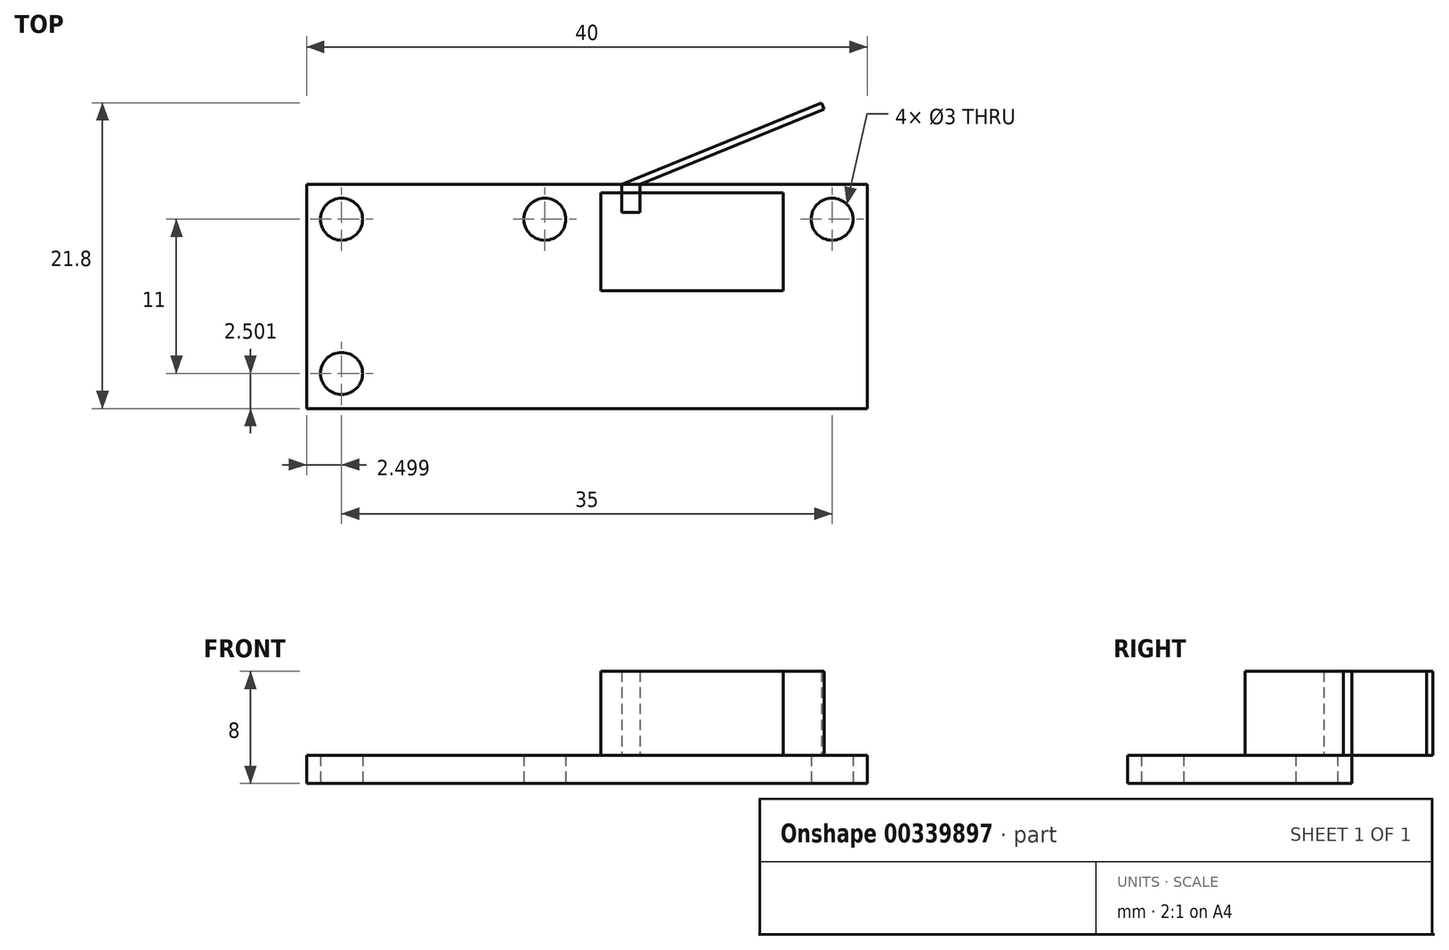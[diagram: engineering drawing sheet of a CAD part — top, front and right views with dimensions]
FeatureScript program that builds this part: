
annotation { "Feature Type Name" : "Feature", "Feature Type Description" : "" }
export const myFeature = defineFeature(function(context is Context, id is Id, definition is map)
    precondition{}
    {
        {
            var Q0;
            Q0=qCreatedBy(makeId("Top.planeOp"),FACE);
            var sketch = newSketch(context, id + "F0", { "sketchPlane" : qUnion([Q0])});
            skLineSegment(sketch, "E0.bottom", {"start": v(-12.98, 9.23) * mm, "end": v(27.02, 9.23) * mm});
            skLineSegment(sketch, "E0.top", {"start": v(-12.98, -6.77) * mm, "end": v(27.02, -6.77) * mm});
            skLineSegment(sketch, "E0.left", {"start": v(-12.98, 9.23) * mm, "end": v(-12.98, -6.77) * mm});
            skLineSegment(sketch, "E0.right", {"start": v(27.02, 9.23) * mm, "end": v(27.02, -6.77) * mm});
            skCircle(sketch, "E1", {"center": v(24.52, 6.73) * mm, "radius": 1.5 * mm});
            skCircle(sketch, "E2", {"center": v(4.02, 6.73) * mm, "radius": 1.5 * mm});
            skCircle(sketch, "E3", {"center": v(-10.48, 6.73) * mm, "radius": 1.5 * mm});
            skCircle(sketch, "E4", {"center": v(-10.48, -4.27) * mm, "radius": 1.5 * mm});
            skLineSegment(sketch, "E5", {"start": v(-12.98, 6.73) * mm, "end": v(27.02, 6.73) * mm, "construction": true});
            skLineSegment(sketch, "E6", {"start": v(-10.48, 9.23) * mm, "end": v(-10.48, -6.77) * mm, "construction": true});
            skSolve(sketch);
        }
        {
            var Q0;
            Q0=makeQuery(id+"F0.imprint","IMPRINT",FACE,{"disambiguationData":[TD([[makeQuery(id+"F0.imprint","IMPRINT",EDGE,{"derivedFrom":sQuery(id+"F0.wireOp",EDGE,"E0.bottom")}),-1.0]])]});
            extrude(context, id + "F1", {"entities" : qUnion([Q0]), "depth" : 2 * mm, "offsetDistance" : 25 * mm});
        }
        {
            var Q0;
            Q0=makeQuery(id+"F1.opExtrude","CAP_FACE",FACE,{"disambiguationData":[OSD([sQuery(id+"F0.wireOp",EDGE,"E0.bottom"),sQuery(id+"F0.wireOp",EDGE,"E0.top"),sQuery(id+"F0.wireOp",EDGE,"E0.left"),sQuery(id+"F0.wireOp",EDGE,"E0.right"),sQuery(id+"F0.wireOp",EDGE,"E1"),sQuery(id+"F0.wireOp",EDGE,"E2"),sQuery(id+"F0.wireOp",EDGE,"E3"),sQuery(id+"F0.wireOp",EDGE,"E4")])],"isStart":false});
            var sketch = newSketch(context, id + "F2", { "sketchPlane" : qUnion([Q0])});
            skLineSegment(sketch, "E7.bottom", {"start": v(8.02, 8.63) * mm, "end": v(21.02, 8.63) * mm});
            skLineSegment(sketch, "E7.top", {"start": v(8.02, 1.63) * mm, "end": v(21.02, 1.63) * mm});
            skLineSegment(sketch, "E7.left", {"start": v(8.02, 8.63) * mm, "end": v(8.02, 1.63) * mm});
            skLineSegment(sketch, "E7.right", {"start": v(21.02, 8.63) * mm, "end": v(21.02, 1.63) * mm});
            skLineSegment(sketch, "E8.bottom", {"start": v(-12.26, 7.1) * mm, "end": v(-2.26, 7.1) * mm});
            skLineSegment(sketch, "E8.top", {"start": v(-12.26, -4.9) * mm, "end": v(-2.26, -4.9) * mm});
            skLineSegment(sketch, "E8.left", {"start": v(-12.26, 7.1) * mm, "end": v(-12.26, -4.9) * mm});
            skLineSegment(sketch, "E8.right", {"start": v(-2.26, 7.1) * mm, "end": v(-2.26, -4.9) * mm});
            skLineSegment(sketch, "E9", {"start": v(8.02, 8.63) * mm, "end": v(23.77, 15.03) * mm});
            skLineSegment(sketch, "E10", {"start": v(23.77, 15.03) * mm, "end": v(23.96, 14.57) * mm});
            skLineSegment(sketch, "E11", {"start": v(23.96, 14.57) * mm, "end": v(9.32, 8.63) * mm});
            skSolve(sketch);
        }
        {
            var Q0;
            {var subQ0=sQuery(id+"F2.wireOp",EDGE,"E8.left");Q0=makeQuery(id+"F2.imprint","IMPRINT",FACE,{"disambiguationData":[TD([[makeQuery(id+"F2.imprint","IMPRINT",EDGE,{"derivedFrom":subQ0}),1.0]])]});}
            var Q1;
            Q1=makeQuery(id+"F2.imprint","IMPRINT",FACE,{"disambiguationData":[TD([[makeQuery(id+"F2.imprint","IMPRINT",EDGE,{"derivedFrom":sQuery(id+"F2.wireOp",EDGE,"E7.bottom")}),-1.0]])]});
            var Q2;
            {var subQ0=sQuery(id+"F2.wireOp",EDGE,"E10");Q2=makeQuery(id+"F2.imprint","IMPRINT",FACE,{"disambiguationData":[TD([[makeQuery(id+"F2.imprint","IMPRINT",EDGE,{"derivedFrom":subQ0}),-1.0]])]});}
            extrude(context, id + "F3", {"entities" : qUnion([Q0, Q1, Q2]), "operationType" : NewBodyOperationType.ADD, "depth" : 6 * mm, "offsetDistance" : 25 * mm});
        }
        {
            var Q0;
            Q0=makeQuery(id+"F3.opExtrude","SWEPT_FACE",FACE,{"disambiguationData":[OSD([sQuery(id+"F0.wireOp",EDGE,"E0.bottom")])]});
            extrude(context, id + "F4", {"entities" : qUnion([Q0]), "depth" : 2 * mm, "offsetDistance" : 25 * mm});
        }
    });
